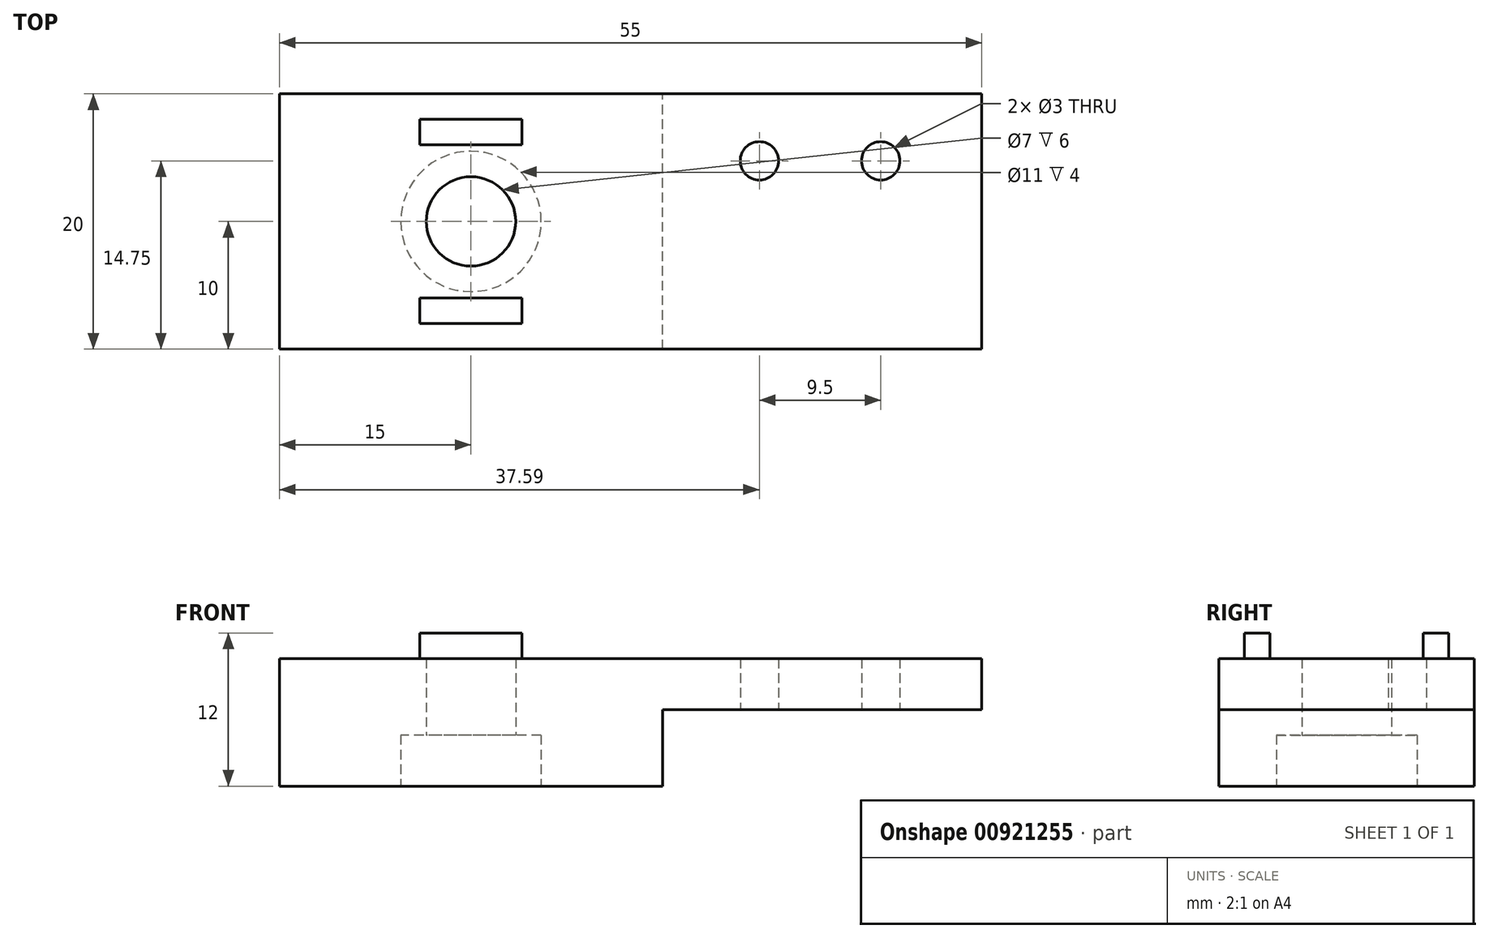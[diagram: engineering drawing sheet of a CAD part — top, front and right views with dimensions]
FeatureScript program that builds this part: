
annotation { "Feature Type Name" : "Feature", "Feature Type Description" : "" }
export const myFeature = defineFeature(function(context is Context, id is Id, definition is map)
    precondition{}
    {
        {
            var Q0;
            Q0=qCreatedBy(makeId("Top.planeOp"),FACE);
            var sketch = newSketch(context, id + "F0", { "sketchPlane" : qUnion([Q0])});
            skLineSegment(sketch, "E0.bottom", {"start": v(27.5, -10) * mm, "end": v(-27.5, -10) * mm});
            skLineSegment(sketch, "E0.top", {"start": v(27.5, 10) * mm, "end": v(-27.5, 10) * mm});
            skLineSegment(sketch, "E0.left", {"start": v(27.5, -10) * mm, "end": v(27.5, 10) * mm});
            skLineSegment(sketch, "E0.right", {"start": v(-27.5, -10) * mm, "end": v(-27.5, 10) * mm});
            skCircle(sketch, "E1", {"center": v(-12.5, 0) * mm, "radius": 3.5 * mm});
            skCircle(sketch, "E2", {"center": v(19.59, 4.75) * mm, "radius": 1.5 * mm});
            skCircle(sketch, "E3", {"center": v(10.1, 4.75) * mm, "radius": 1.5 * mm});
            skSolve(sketch);
        }
        {
            var Q0;
            Q0 = qSketchRegion(id + "F0", true);
            extrude(context, id + "F1", {"entities" : qUnion([Q0]), "depth" : 10 * mm, "offsetDistance" : 25 * mm});
        }
        {
            var Q0;
            Q0=makeQuery(id+"F1.opExtrude","CAP_FACE",FACE,{"disambiguationData":[OSD([sQuery(id+"F0.wireOp",EDGE,"E0.bottom"),sQuery(id+"F0.wireOp",EDGE,"E0.top"),sQuery(id+"F0.wireOp",EDGE,"E0.left"),sQuery(id+"F0.wireOp",EDGE,"E0.right"),sQuery(id+"F0.wireOp",EDGE,"E1"),sQuery(id+"F0.wireOp",EDGE,"E2"),sQuery(id+"F0.wireOp",EDGE,"14b4ebb8-f1cd-40d1-ad0a-c5b000fb0263")])],"isStart":false});
            var sketch = newSketch(context, id + "F2", { "sketchPlane" : qUnion([Q0])});
            skLineSegment(sketch, "E4.bottom", {"start": v(-16.5, 8) * mm, "end": v(-8.5, 8) * mm});
            skLineSegment(sketch, "E4.top", {"start": v(-16.5, 6) * mm, "end": v(-8.5, 6) * mm});
            skLineSegment(sketch, "E4.left", {"start": v(-16.5, 8) * mm, "end": v(-16.5, 6) * mm});
            skLineSegment(sketch, "E4.right", {"start": v(-8.5, 8) * mm, "end": v(-8.5, 6) * mm});
            skLineSegment(sketch, "E5.bottom", {"start": v(-16.5, -6) * mm, "end": v(-8.5, -6) * mm});
            skLineSegment(sketch, "E5.top", {"start": v(-16.5, -8) * mm, "end": v(-8.5, -8) * mm});
            skLineSegment(sketch, "E5.left", {"start": v(-16.5, -6) * mm, "end": v(-16.5, -8) * mm});
            skLineSegment(sketch, "E5.right", {"start": v(-8.5, -6) * mm, "end": v(-8.5, -8) * mm});
            skSolve(sketch);
        }
        {
            var Q0;
            Q0=makeQuery(id+"F2.imprint","IMPRINT",FACE,{"disambiguationData":[TD([[makeQuery(id+"F2.imprint","IMPRINT",EDGE,{"derivedFrom":sQuery(id+"F2.wireOp",EDGE,"E4.bottom")}),-1.0]])]});
            var Q1;
            Q1=makeQuery(id+"F2.imprint","IMPRINT",FACE,{"disambiguationData":[TD([[makeQuery(id+"F2.imprint","IMPRINT",EDGE,{"derivedFrom":sQuery(id+"F2.wireOp",EDGE,"E5.bottom")}),-1.0]])]});
            extrude(context, id + "F3", {"entities" : qUnion([Q0, Q1]), "operationType" : NewBodyOperationType.ADD, "depth" : 2 * mm, "offsetDistance" : 25 * mm});
        }
        {
            var Q0;
            Q0=qCreatedBy(makeId("Top.planeOp"),FACE);
            var sketch = newSketch(context, id + "F4", { "sketchPlane" : qUnion([Q0])});
            skCircle(sketch, "E6", {"center": v(-12.5, 0) * mm, "radius": 5.5 * mm});
            skSolve(sketch);
        }
        {
            var Q0;
            Q0=makeQuery(id+"F4.imprint","IMPRINT",FACE,{"disambiguationData":[TD([[makeQuery(id+"F4.imprint","IMPRINT",EDGE,{"derivedFrom":sQuery(id+"F4.wireOp",EDGE,"E6")}),1.0]])]});
            extrude(context, id + "F5", {"entities" : qUnion([Q0]), "operationType" : NewBodyOperationType.REMOVE, "oppositeDirection" : true, "depth" : -4 * mm, "offsetDistance" : 25 * mm});
        }
        {
            var Q0;
            Q0=qCreatedBy(makeId("Top.planeOp"),FACE);
            var sketch = newSketch(context, id + "F6", { "sketchPlane" : qUnion([Q0])});
            skLineSegment(sketch, "E7.bottom", {"start": v(2.5, -10) * mm, "end": v(27.5, -10) * mm});
            skLineSegment(sketch, "E7.top", {"start": v(2.5, 10) * mm, "end": v(27.5, 10) * mm});
            skLineSegment(sketch, "E7.left", {"start": v(2.5, -10) * mm, "end": v(2.5, 10) * mm});
            skLineSegment(sketch, "E7.right", {"start": v(27.5, -10) * mm, "end": v(27.5, 10) * mm});
            skSolve(sketch);
        }
        {
            var Q0;
            Q0=makeQuery(id+"F6.imprint","IMPRINT",FACE,{"disambiguationData":[TD([[makeQuery(id+"F6.imprint","IMPRINT",EDGE,{"derivedFrom":sQuery(id+"F6.wireOp",EDGE,"E7.bottom")}),1.0]])]});
            extrude(context, id + "F7", {"entities" : qUnion([Q0]), "operationType" : NewBodyOperationType.REMOVE, "depth" : 6 * mm, "offsetDistance" : 25 * mm});
        }
    });
